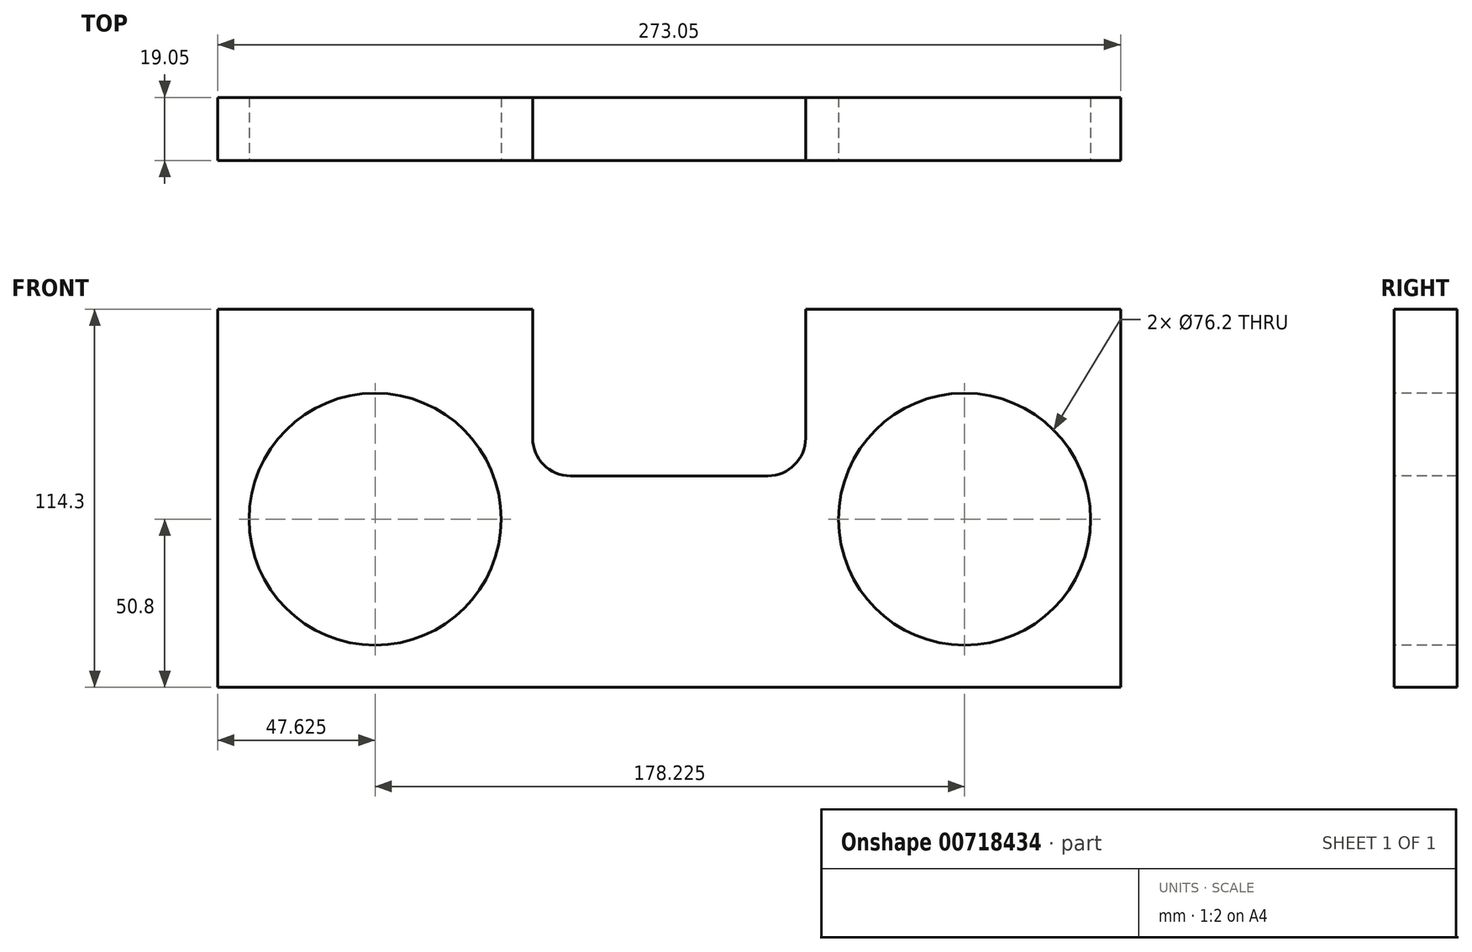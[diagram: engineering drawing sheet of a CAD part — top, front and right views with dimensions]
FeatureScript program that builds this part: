
annotation { "Feature Type Name" : "Feature", "Feature Type Description" : "" }
export const myFeature = defineFeature(function(context is Context, id is Id, definition is map)
    precondition{}
    {
        {
            var Q0;
            Q0=qCreatedBy(makeId("Front.planeOp"),FACE);
            var sketch = newSketch(context, id + "F0", { "sketchPlane" : qUnion([Q0])});
            skLineSegment(sketch, "E0.bottom", {"start": v(0, 0) * mm, "end": v(273.05, 0) * mm});
            skLineSegment(sketch, "E0.top", {"start": v(0, 114.3) * mm, "end": v(273.05, 114.3) * mm});
            skLineSegment(sketch, "E0.left", {"start": v(0, 0) * mm, "end": v(0, 114.3) * mm});
            skLineSegment(sketch, "E0.right", {"start": v(273.05, 0) * mm, "end": v(273.05, 114.3) * mm});
            skSolve(sketch);
        }
        {
            var Q0;
            Q0 = qSketchRegion(id + "F0", true);
            extrude(context, id + "F1", {"entities" : qUnion([Q0]), "depth" : 19.05 * mm, "offsetDistance" : 25.4 * mm});
        }
        {
            var Q0;
            Q0=makeQuery(id+"F1.opExtrude","CAP_FACE",FACE,{"disambiguationData":[OSD([sQuery(id+"F0.wireOp",EDGE,"E0.bottom"),sQuery(id+"F0.wireOp",EDGE,"E0.top"),sQuery(id+"F0.wireOp",EDGE,"E0.left"),sQuery(id+"F0.wireOp",EDGE,"E0.right")])],"isStart":false});
            var sketch = newSketch(context, id + "F2", { "sketchPlane" : qUnion([Q0])});
            skCircle(sketch, "E1", {"center": v(47.63, 50.8) * mm, "radius": 38.1 * mm});
            skCircle(sketch, "E2", {"center": v(225.85, 50.8) * mm, "radius": 38.1 * mm});
            skLineSegment(sketch, "E3", {"start": v(95.25, 114.3) * mm, "end": v(95.25, 75.35) * mm});
            skLineSegment(sketch, "E4", {"start": v(106.68, 63.92) * mm, "end": v(166.37, 63.92) * mm});
            skLineSegment(sketch, "E5", {"start": v(177.8, 75.35) * mm, "end": v(177.8, 114.3) * mm});
            skPoint(sketch, "E6.visualSharp", {"position": v(95.25, 63.92) * mm});
            skArc(sketch, "E6.filletArc", {"start": v(95.25, 75.35) * mm, "mid": v(98.6, 67.27) * mm, "end": v(106.68, 63.92) * mm});
            skPoint(sketch, "E7.visualSharp", {"position": v(177.8, 63.92) * mm});
            skArc(sketch, "E7.filletArc", {"start": v(166.37, 63.92) * mm, "mid": v(174.45, 67.27) * mm, "end": v(177.8, 75.35) * mm});
            skSolve(sketch);
        }
        {
            var Q0;
            Q0=makeQuery(id+"F2.imprint","IMPRINT",FACE,{"disambiguationData":[TD([[makeQuery(id+"F2.imprint","IMPRINT",EDGE,{"derivedFrom":sQuery(id+"F2.wireOp",EDGE,"E2")}),1.0]])]});
            var Q1;
            {var subQ0=sQuery(id+"F2.wireOp",EDGE,"E3");Q1=makeQuery(id+"F2.imprint","IMPRINT",FACE,{"disambiguationData":[TD([[makeQuery(id+"F2.imprint","IMPRINT",EDGE,{"derivedFrom":subQ0}),1.0]])]});}
            var Q2;
            Q2=makeQuery(id+"F2.imprint","IMPRINT",FACE,{"disambiguationData":[TD([[makeQuery(id+"F2.imprint","IMPRINT",EDGE,{"derivedFrom":sQuery(id+"F2.wireOp",EDGE,"E1")}),1.0]])]});
            extrude(context, id + "F3", {"entities" : qUnion([Q0, Q1, Q2]), "operationType" : NewBodyOperationType.REMOVE, "oppositeDirection" : true, "depth" : 25.4 * mm, "offsetDistance" : 25.4 * mm});
        }
    });
